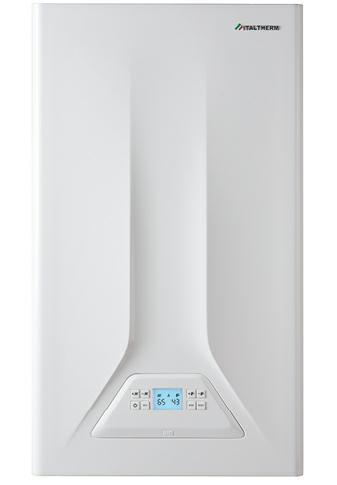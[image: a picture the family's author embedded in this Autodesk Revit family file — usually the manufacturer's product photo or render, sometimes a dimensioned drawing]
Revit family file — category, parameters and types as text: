
# Revit family: City Top Muro
name_source: partatom
category: Attrezzatura meccanica
units: mm (PartAtom-declared; Revit-internal decimal feet)

## family parameters
Classificazione = Nessuno
Condiviso = No
Host = Muro
Punto di calcolo locali = No
Quota connettore circolare = Usa diametro
Sempre verticale = Sì
Taglio con vuoti quando caricato = No
Tipo di parte = Normale

## types (2) — shared parameters
Date of publishing = 12/09/2019
Depth = 324 mm  [stored 1.06299 ft]
Design country = Italy
Domestic Cold Water Diameter = 21 mm  [stored 0.0688976 ft]
Domestic Hot Water Diameter = 21 mm  [stored 0.0688976 ft]
Energetic efficiency (92/42/CEE) = n.d.
Flue outlet = 100 mm  [stored 0.328084 ft]
Gas Inlet Diameter = 26 mm
Height = 700 mm  [stored 2.29659 ft]
Hydronic Return Diameter = 26 mm
Hydronic Supply Diameter = 26 mm
IFC Classification = Boiler
Immagine tipo = city top.jpg
Manufacturer country = Italy
Manufacturer name = Italtherm S.p.A.
Material main = Metal
Material secondary = Plastic
Minimum heat output 50/30°C = 2 W
Minimum heat output 80/60°C = 2 W
NBS reference Description = Boilers
Omniclass Description = Condensing boilers
Power consumption (W) = 86 W
Power supply | Frequency (Hz) = 50 Hz
Power supply | Phase = 1
Power supply | Voltage (V) = 230 V
Product family = Heating
Product group = Thermal unit
Siphon with condensate drain = 25 mm  [stored 0.082021 ft]
Uniclass 2015 Name = Boilers
Weight = 36.80 kg
Width = 400 mm  [stored 1.31234 ft]
zero-valued in all types: Edition number, Prospetto di default

## per-type parameters (varying)
| type | Efficiency 30% | Maximum heat output 50/30°C | Maximum heat output 80/60°C | Maximum heating heat input | Nominal efficiency 50/30°C | Nominal efficiency 80/60°C | URL | URL ENG |
| 25K | 105.30% | 27 W | 24 W | 25 W | 104.40% | 96.20% | www.italtherm.it/g/caldaia-a-gas-da-interno/caldaia-a-condensazione/city-top-k/25-kw | en.italtherm.it/g/wall-hung-condensing-boilers/gas-boiler/city-top-k/25-kw |
| 35K | 105.60% | 35 W | 32 W | 33 W | 105.10% | 97.10% | www.italtherm.it/g/caldaia-a-gas-da-interno/caldaia-a-condensazione/city-top-k/35-kw | en.italtherm.it/g/wall-hung-condensing-boilers/gas-boiler/city-top-k/35-kw |

note: [stored X ft] marks values corroborated as IEEE doubles in the binary element streams (Revit-internal decimal feet)
